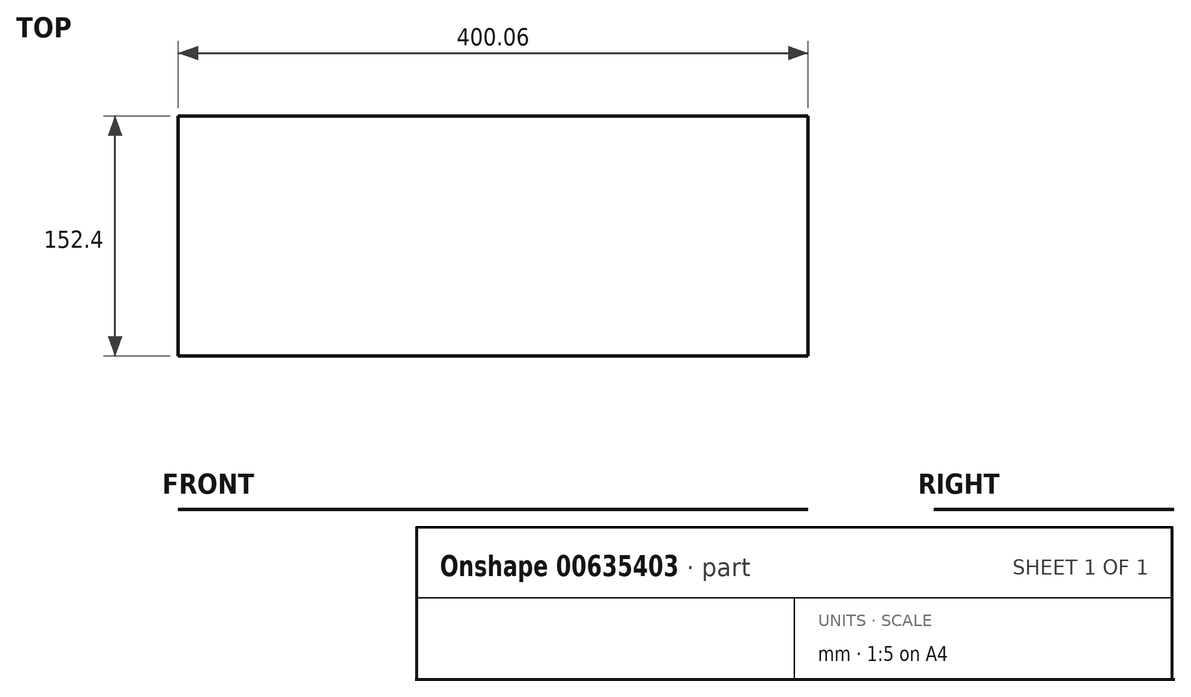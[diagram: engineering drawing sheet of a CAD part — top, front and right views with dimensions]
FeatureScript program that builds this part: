
annotation { "Feature Type Name" : "Feature", "Feature Type Description" : "" }
export const myFeature = defineFeature(function(context is Context, id is Id, definition is map)
    precondition{}
    {
        {
            var Q0;
            Q0=qCreatedBy(makeId("Top.planeOp"),FACE);
            var sketch = newSketch(context, id + "F0", { "sketchPlane" : qUnion([Q0])});
            skLineSegment(sketch, "E0.bottom", {"start": v(-200.03, 76.2) * mm, "end": v(200.03, 76.2) * mm});
            skLineSegment(sketch, "E0.top", {"start": v(-200.03, -76.2) * mm, "end": v(200.03, -76.2) * mm});
            skLineSegment(sketch, "E0.left", {"start": v(-200.02, 76.2) * mm, "end": v(-200.03, -76.2) * mm});
            skLineSegment(sketch, "E0.right", {"start": v(200.03, 76.2) * mm, "end": v(200.03, -76.2) * mm});
            skPoint(sketch, "E0.middle", {"position": v(0, 0) * mm});
            skSolve(sketch);
        }
        {
            var Q0;
            Q0=qSketchRegion(id+"F0",true);
            extrude(context, id + "F1", {"entities" : qUnion([Q0]), "depth" : 1 / 203.2 * mm});
        }
    });
